# Revit family: 306_72df8b94579342c6a6a20826c9b745
name_source: partatom
category: Pipe Accessories
units: mm (PartAtom-declared; Revit-internal decimal feet)

## family parameters
Always vertical = Yes
Cut with Voids When Loaded = No
Part Type = Valve - Breaks Into
Round Connector Dimension = Use Diameter
Shared = No
Work Plane-Based = No

## types (2) — shared parameters
Description = 3-way Motorized ball valve MBA132, PN32 external thread
H1 = 1 mm  [stored 0.00328084 ft]
L2D_Min = 3048 mm  [stored 10 ft]
MC = No
Manufacturer = ESBE
QmdConnectorList = 301;D;302;D
URL = http://www.esbe.eu
X6 = 6 mm  [stored 0.019685 ft]
X6__ve = -6 mm  [stored -0.019685 ft]
Y0 = 5 mm  [stored 0.0164042 ft]
Y11 = 3 mm  [stored 0.00984252 ft]
Z1 = 19 mm  [stored 0.062336 ft]
Z1__ve = -19 mm
Z3 = 11 mm
Z4 = 52 mm
Z5 = 3 mm  [stored 0.00984252 ft]
Z6 = 35 mm
Z6__ve = -35 mm
Z7 = 3 mm  [stored 0.00984252 ft]
magiPartTypeId = 306
magiProductFamilyId = 72df8b94579342c6a6a20826c9b745

## per-type parameters (varying)
- MBA132 G1  MMM 230VAC 2-P 10NM: D=25 mm; E=25 mm  [stored 0.082021 ft]; H=34 mm; L2D=60 mm; W2D=25 mm  [stored 0.082021 ft]; X1=36 mm  [stored 0.11811 ft]; X12=22 mm; X12__ve=-22 mm; X13=29 mm; X14=30 mm  [stored 0.0984252 ft]; X5=2 mm  [stored 0.00656168 ft]; X7=5 mm  [stored 0.0164042 ft]; X8=11 mm; X8__ve=-11 mm; X9=19 mm  [stored 0.062336 ft]; Y1=13 mm  [stored 0.0426509 ft]; Y10=19 mm  [stored 0.062336 ft]; Y10__ve=-19 mm; Y12=12 mm  [stored 0.0393701 ft]; Y3=14 mm  [stored 0.0459318 ft]; Y4=13 mm  [stored 0.0426509 ft]; Y5=14 mm  [stored 0.0459318 ft]; Z2=23 mm; Z8=30 mm  [stored 0.0984252 ft]; magiProductCode=MBA132 G1" MMM 230VAC 2-P 10NM; magiProductId=c14969e717cd45528d98066227186a
- MBA132 G11/4  MMM 230VAC 2-P 10NM: D=32 mm; E=29 mm; H=40 mm; L2D=70 mm; W2D=32 mm; X1=41 mm; X12=26 mm  [stored 0.0853018 ft]; X12__ve=-26 mm; X13=34 mm; X14=35 mm; X5=3 mm  [stored 0.00984252 ft]; X7=6 mm  [stored 0.019685 ft]; X8=13 mm  [stored 0.0426509 ft]; X8__ve=-13 mm  [stored -0.0426509 ft]; X9=22 mm; Y1=16 mm; Y10=24 mm; Y10__ve=-24 mm; Y12=16 mm; Y3=18 mm  [stored 0.0590551 ft]; Y4=17 mm; Y5=17 mm; Z2=26 mm  [stored 0.0853018 ft]; Z8=33 mm  [stored 0.108268 ft]; magiProductCode=MBA132 G11/4" MMM 230VAC 2-P 10NM; magiProductId=57c77bde6c2f46ed97683d46723ae1

note: [stored X ft] marks values corroborated as IEEE doubles in the binary element streams (Revit-internal decimal feet)

## geometry (parser evidence)
native form markers: Sweep x3
no freeform markers — native parametric forms only
